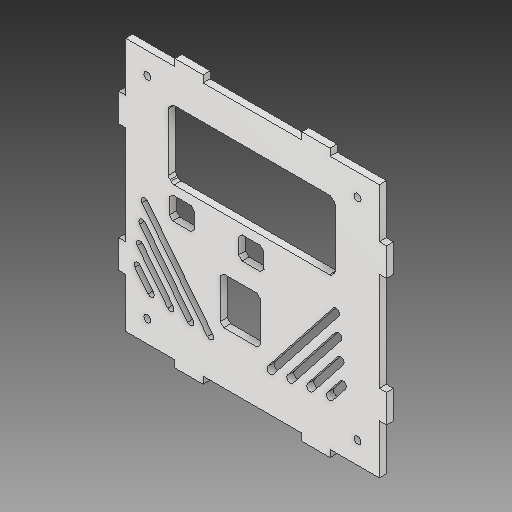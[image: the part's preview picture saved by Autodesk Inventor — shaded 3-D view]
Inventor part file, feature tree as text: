
AUTODESK INVENTOR PART (.ipt)
format: ipt  version: 2018.2 (Build 222227000, 227)  size: 275,456 bytes
history: native  units: in
note: dims shown in document units (in); Inventor stores cm internally (conversion verified against a paired STEP export)
features: extrude x1, sketch x1
ambient origin geometry x8: Origin, YZ Plane, XZ Plane, XY Plane, X Axis, Y Axis, Z Axis, Center Point
bodies: Solid1 (feature_tree)
feature tree (2):
  extrude  "Extrusion1"  Depth=0.715in
  sketch  "Sketch1"  dims[d1=0.825in d2=0.715in d3=0.0625in d4=0.0625in d5=0.0625in d6=0.0625in d7=0.0625in d8=0.0625in d9=0.0625in d10=0.0625in d11=0.45in d12=0.0in d13=0.4in d14=0.45in d15=0.0625in d16=0.0625in d17=0.0625in d18=0.0625in d19=0.0625in d20=0.0625in d21=0.0625in d22=0.0625in d23=0.0625in d24=0.0625in d25=0.0625in d26=0.0625in d27=0.0625in d28=0.0625in d29=0.0625in d30=0.0625in d31=0.125in d32=0.0in d36=0.125in d38=0.5in d39=0.125in d40=0.5in d41=0.125in d42=0.5in d43=0.875in d44=0.125in d45=0.5in d46=0.875in d48=0.5in d49=0.125in d50=0.5in]
